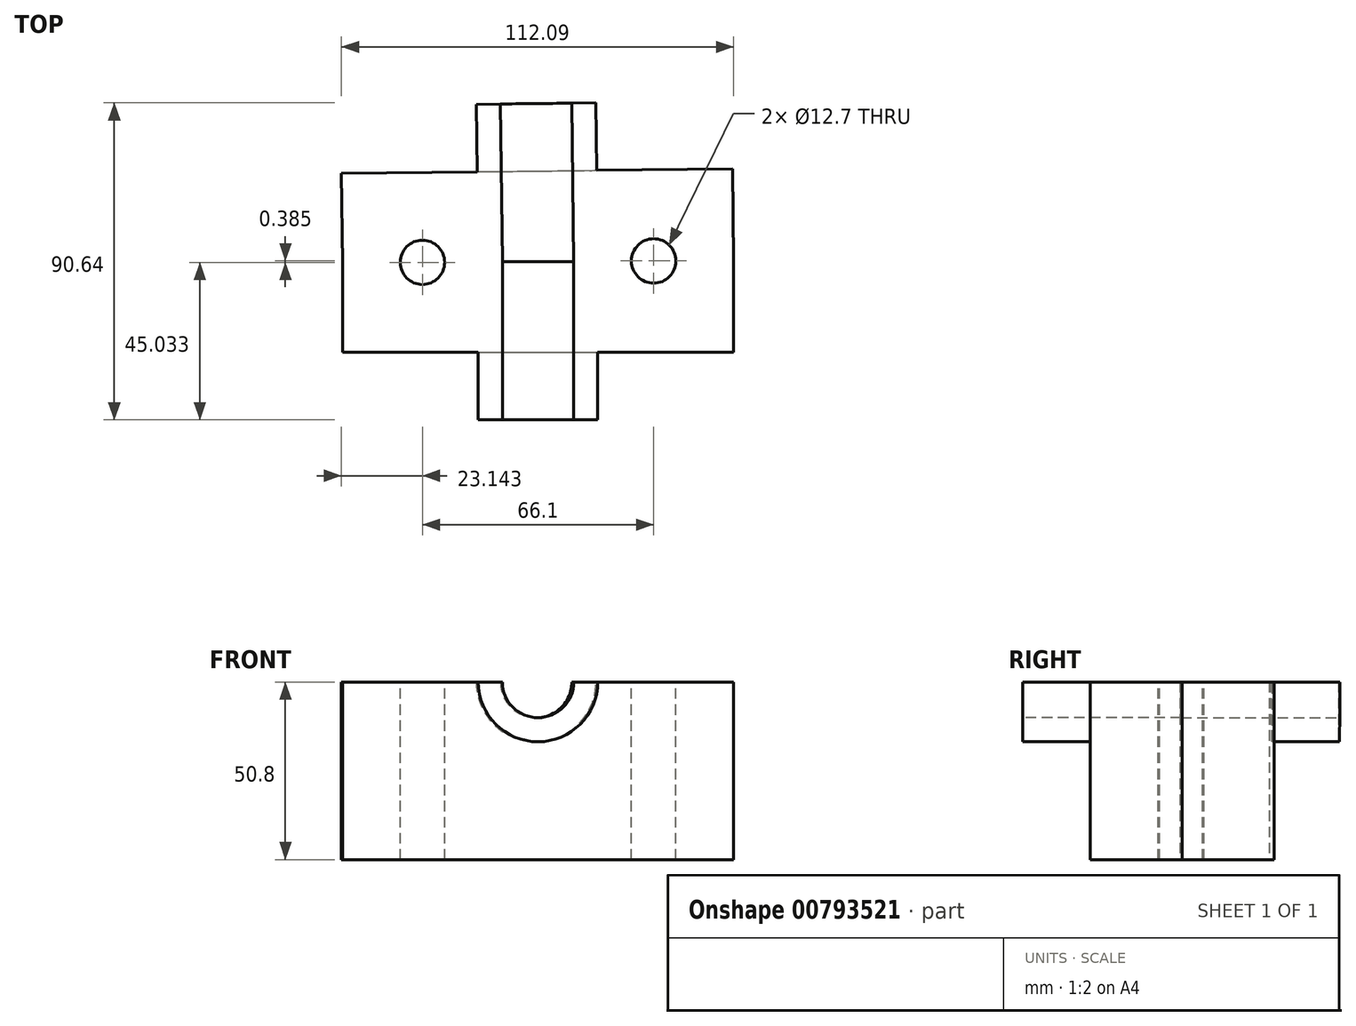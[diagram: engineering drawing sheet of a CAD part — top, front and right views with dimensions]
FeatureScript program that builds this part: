
annotation { "Feature Type Name" : "Feature", "Feature Type Description" : "" }
export const myFeature = defineFeature(function(context is Context, id is Id, definition is map)
    precondition{}
    {
        {
            var Q0;
            Q0=qCreatedBy(makeId("Top.planeOp"),FACE);
            var sketch = newSketch(context, id + "F0", { "sketchPlane" : qUnion([Q0])});
            skLineSegment(sketch, "E0.top", {"start": v(-50.17, -25.6) * mm, "end": v(61.62, -25.6) * mm});
            skLineSegment(sketch, "E0.left", {"start": v(-50.17, 0) * mm, "end": v(-50.17, -25.6) * mm});
            skLineSegment(sketch, "E0.right", {"start": v(61.62, 0.65) * mm, "end": v(61.62, -25.6) * mm});
            skLineSegment(sketch, "E1", {"start": v(-50.17, 0) * mm, "end": v(61.62, 0.65) * mm});
            skPoint(sketch, "E2.orphan", {"position": v(61.62, 26.9) * mm});
            skSolve(sketch);
        }
        {
            var Q0;
            Q0=makeQuery(id+"F0.imprint","IMPRINT",FACE,{"disambiguationData":[TD([[makeQuery(id+"F0.imprint","IMPRINT",EDGE,{"derivedFrom":sQuery(id+"F0.wireOp",EDGE,"E0.top")}),1.0]])]});
            extrude(context, id + "F1", {"entities" : qUnion([Q0]), "depth" : 50.8 * mm, "offsetDistance" : 25.4 * mm});
        }
        {
            var Q0;
            Q0=makeQuery(id+"F1.opExtrude","SWEPT_FACE",FACE,{"disambiguationData":[OSD([sQuery(id+"F0.wireOp",EDGE,"E0.top")])]});
            var sketch = newSketch(context, id + "F2", { "sketchPlane" : qUnion([Q0])});
            skArc(sketch, "E3", {"start": v(-11.37, 50.8) * mm, "mid": v(5.72, 33.7) * mm, "end": v(22.82, 50.8) * mm});
            skArc(sketch, "E4", {"start": v(-4.48, 50.8) * mm, "mid": v(5.72, 40.6) * mm, "end": v(15.93, 50.8) * mm});
            skSolve(sketch);
        }
        {
            var Q0;
            {var subQ0=sQuery(id+"F2.wireOp",EDGE,"E4");Q0=makeQuery(id+"F2.imprint","IMPRINT",FACE,{"disambiguationData":[TD([[makeQuery(id+"F2.imprint","IMPRINT",EDGE,{"derivedFrom":subQ0}),1.0]])]});}
            extrude(context, id + "F3", {"entities" : qUnion([Q0]), "operationType" : NewBodyOperationType.REMOVE, "oppositeDirection" : true, "depth" : 33.78 * mm, "offsetDistance" : 25.4 * mm});
        }
        {
            var Q0;
            {var subQ0=sQuery(id+"F2.wireOp",EDGE,"E3");Q0=makeQuery(id+"F2.imprint","IMPRINT",FACE,{"disambiguationData":[TD([[makeQuery(id+"F2.imprint","IMPRINT",EDGE,{"derivedFrom":subQ0}),1.0]])]});}
            extrude(context, id + "F4", {"entities" : qUnion([Q0]), "operationType" : NewBodyOperationType.ADD, "depth" : 19.3 * mm, "offsetDistance" : 25.4 * mm});
        }
        {
            var Q0;
            {var subQ0=sQuery(id+"F0.wireOp",EDGE,"E0.top");var subQ1=makeQuery(id+"F1.opExtrude","CAP_EDGE",EDGE,{"disambiguationData":[OSD([subQ0])],"isStart":false});var subQ3=sQuery(id+"F0.wireOp",EDGE,"E1");var subQ4=sQuery(id+"F0.wireOp",EDGE,"E0.left");Q0=makeQuery(id+"F4.boolean.opBoolean","MERGE",FACE,{"derivedFrom":[makeQuery(id+"F3.boolean.opBoolean","SPLIT",FACE,{"disambiguationData":[TD([makeQuery(id+"F1.opExtrude","SWEPT_FACE",FACE,{"disambiguationData":[OSD([subQ4])]})])],"derivedFrom":makeQuery(id+"F1.opExtrude","CAP_FACE",FACE,{"disambiguationData":[OSD([subQ0,subQ4,sQuery(id+"F0.wireOp",EDGE,"E0.right"),subQ3])],"isStart":false})}),makeQuery(id+"F4.opExtrude","SWEPT_FACE",FACE,{"disambiguationData":[OSD([subQ0]),TDD([makeQuery(id+"F2.imprint","IMPRINT",EDGE,{"disambiguationData":[TD([[makeQuery(id+"F2.imprint","INTERSECT",VERTEX,{"disambiguationData":[OD(0.0)],"derivedFrom":[subQ1,sQuery(id+"F2.wireOp",EDGE,"E3")]}),-1.0]])],"derivedFrom":subQ1})])]})]});}
            var sketch = newSketch(context, id + "F5", { "sketchPlane" : qUnion([Q0])});
            skArc(sketch, "E5", {"start": v(-33.68, 0.1) * mm, "mid": v(-27.3, -6.22) * mm, "end": v(-20.98, 0.17) * mm});
            skSolve(sketch);
        }
        {
            var Q0;
            {var subQ0=sQuery(id+"F0.wireOp",EDGE,"E0.top");var subQ1=makeQuery(id+"F1.opExtrude","CAP_EDGE",EDGE,{"disambiguationData":[OSD([subQ0])],"isStart":false});var subQ3=sQuery(id+"F0.wireOp",EDGE,"E1");var subQ4=sQuery(id+"F0.wireOp",EDGE,"E0.right");Q0=makeQuery(id+"F4.boolean.opBoolean","MERGE",FACE,{"derivedFrom":[makeQuery(id+"F3.boolean.opBoolean","SPLIT",FACE,{"disambiguationData":[TD([makeQuery(id+"F1.opExtrude","SWEPT_FACE",FACE,{"disambiguationData":[OSD([subQ4])]})])],"derivedFrom":makeQuery(id+"F1.opExtrude","CAP_FACE",FACE,{"disambiguationData":[OSD([subQ0,sQuery(id+"F0.wireOp",EDGE,"E0.left"),subQ4,subQ3])],"isStart":false})}),makeQuery(id+"F4.opExtrude","SWEPT_FACE",FACE,{"disambiguationData":[OSD([subQ0]),TDD([makeQuery(id+"F2.imprint","IMPRINT",EDGE,{"disambiguationData":[TD([[makeQuery(id+"F2.imprint","INTERSECT",VERTEX,{"disambiguationData":[OD(1.0)],"derivedFrom":[subQ1,sQuery(id+"F2.wireOp",EDGE,"E3")]}),1.0]])],"derivedFrom":subQ1})])]})]});}
            var sketch = newSketch(context, id + "F6", { "sketchPlane" : qUnion([Q0])});
            skArc(sketch, "E6", {"start": v(32.42, 0.48) * mm, "mid": v(38.8, -5.83) * mm, "end": v(45.12, 0.55) * mm});
            skSolve(sketch);
        }
        {
            var Q0;
            {var subQ0=sQuery(id+"F5.wireOp",EDGE,"E5");Q0=makeQuery(id+"F5.imprint","IMPRINT",FACE,{"disambiguationData":[TD([[makeQuery(id+"F5.imprint","IMPRINT",EDGE,{"derivedFrom":subQ0}),1.0]])]});}
            extrude(context, id + "F7", {"entities" : qUnion([Q0]), "operationType" : NewBodyOperationType.REMOVE, "oppositeDirection" : true, "depth" : 62.74 * mm, "offsetDistance" : 25.4 * mm});
        }
        {
            var Q0;
            {var subQ0=sQuery(id+"F6.wireOp",EDGE,"E6");Q0=makeQuery(id+"F6.imprint","IMPRINT",FACE,{"disambiguationData":[TD([[makeQuery(id+"F6.imprint","IMPRINT",EDGE,{"derivedFrom":subQ0}),1.0]])]});}
            extrude(context, id + "F8", {"entities" : qUnion([Q0]), "operationType" : NewBodyOperationType.REMOVE, "oppositeDirection" : true, "depth" : 50.8 * mm, "offsetDistance" : 25.4 * mm});
        }
        {
            var Q0;
            Q0=makeQuery(id+"F1.opExtrude","SWEPT_BODY",BODY,{"disambiguationData":[OSD([sQuery(id+"F0.wireOp",EDGE,"E0.top"),sQuery(id+"F0.wireOp",EDGE,"E0.left"),sQuery(id+"F0.wireOp",EDGE,"E0.right"),sQuery(id+"F0.wireOp",EDGE,"E1")])]});
            var Q1;
            {var subQ0=sQuery(id+"F2.wireOp",EDGE,"E4");var subQ2=sQuery(id+"F0.wireOp",EDGE,"E1");var subQ3=sQuery(id+"F0.wireOp",EDGE,"E0.right");var subQ7=makeQuery(id+"F3.boolean.opBoolean","COPY",FACE,{"derivedFrom":makeQuery(id+"F3.opExtrude","SWEPT_FACE",FACE,{"disambiguationData":[OSD([subQ0])]})});Q1=makeQuery(id+"F8.boolean.opBoolean","SPLIT",FACE,{"disambiguationData":[TD([subQ7])],"derivedFrom":makeQuery(id+"F7.boolean.opBoolean","SPLIT",FACE,{"disambiguationData":[TD([makeQuery(id+"F1.opExtrude","SWEPT_FACE",FACE,{"disambiguationData":[OSD([subQ3])]})])],"derivedFrom":makeQuery(id+"F1.opExtrude","SWEPT_FACE",FACE,{"disambiguationData":[OSD([subQ2])]})})});}
            mirror(context, id + "F9", {"operationType" : NewBodyOperationType.ADD, "entities" : qUnion([Q0]), "mirrorPlane" : qUnion([Q1])});
        }
    });
